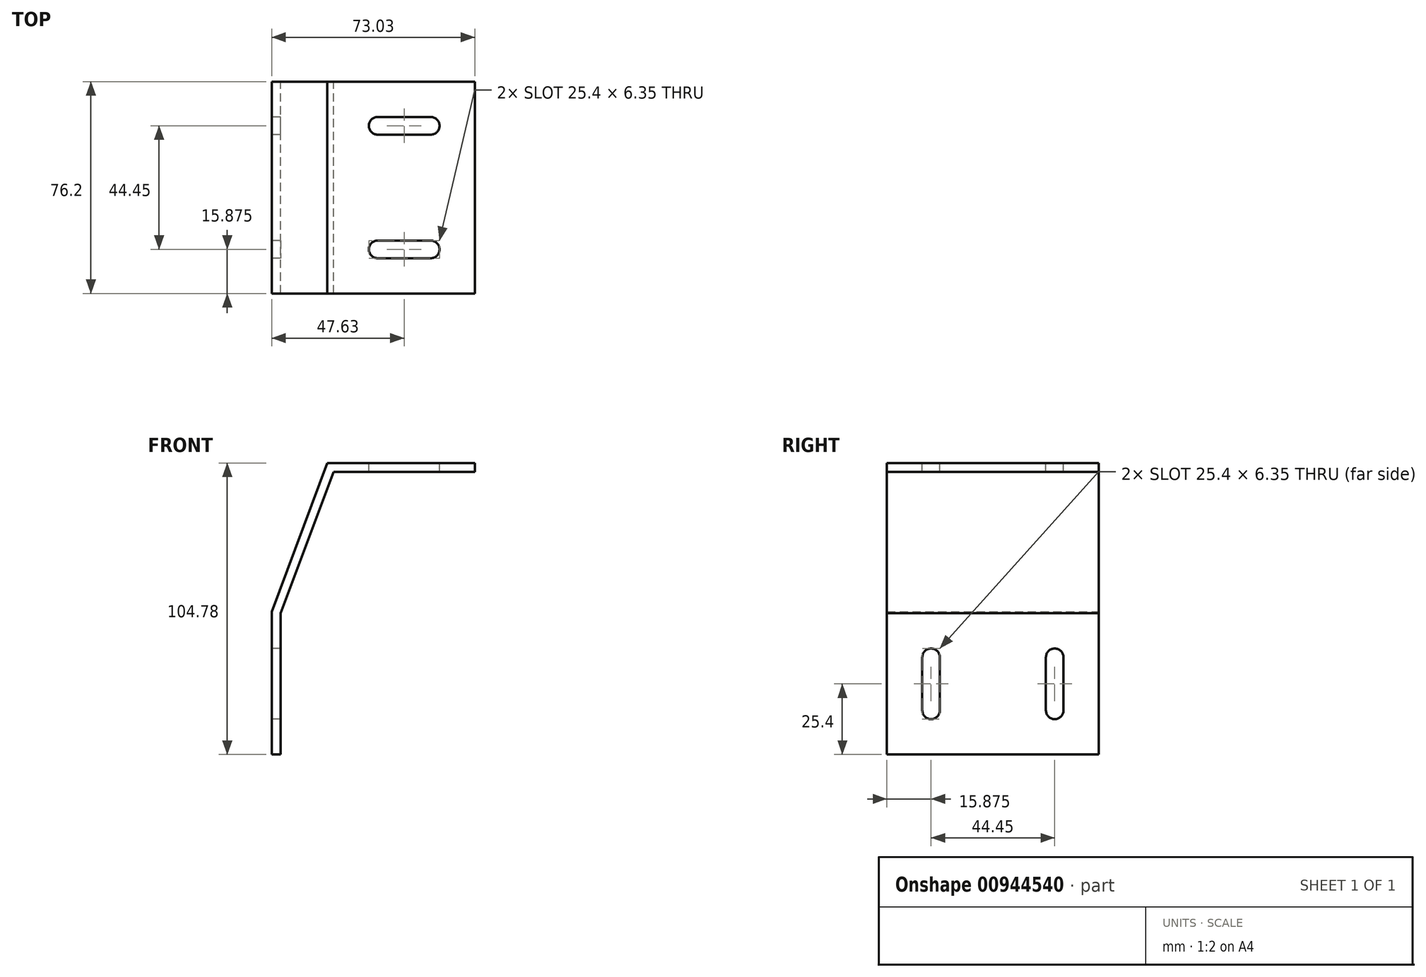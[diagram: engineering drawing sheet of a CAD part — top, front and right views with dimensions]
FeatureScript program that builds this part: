
annotation { "Feature Type Name" : "Feature", "Feature Type Description" : "" }
export const myFeature = defineFeature(function(context is Context, id is Id, definition is map)
    precondition{}
    {
        {
            var Q0;
            Q0=qCreatedBy(makeId("Front.planeOp"),FACE);
            var sketch = newSketch(context, id + "F0", { "sketchPlane" : qUnion([Q0])});
            skLineSegment(sketch, "E0", {"start": v(0, 0) * mm, "end": v(0, -50.8) * mm});
            skLineSegment(sketch, "E1", {"start": v(19.05, 50.8) * mm, "end": v(69.85, 50.8) * mm});
            skLineSegment(sketch, "E2", {"start": v(19.05, 50.8) * mm, "end": v(0, 0) * mm});
            skLineSegment(sketch, "E3", {"start": v(69.85, 50.8) * mm, "end": v(69.85, 53.98) * mm});
            skLineSegment(sketch, "E4", {"start": v(69.85, 53.98) * mm, "end": v(16.85, 53.98) * mm});
            skLineSegment(sketch, "E5", {"start": v(0, -50.8) * mm, "end": v(-3.18, -50.8) * mm});
            skLineSegment(sketch, "E6", {"start": v(-3.18, -50.8) * mm, "end": v(-3.18, 0.58) * mm});
            skLineSegment(sketch, "E7", {"start": v(-3.18, 0.58) * mm, "end": v(16.85, 53.98) * mm});
            skSolve(sketch);
        }
        {
            var Q0;
            Q0=qSketchRegion(id+"F0",true);
            extrude(context, id + "F1", {"entities" : qUnion([Q0]), "depth" : 76.2 * mm, "offsetDistance" : 25.4 * mm});
        }
        {
            var Q0;
            Q0=makeQuery(id+"F1.opExtrude","SWEPT_FACE",FACE,{"disambiguationData":[OSD([sQuery(id+"F0.wireOp",EDGE,"E4")])]});
            var sketch = newSketch(context, id + "F2", { "sketchPlane" : qUnion([Q0])});
            skCircle(sketch, "E8", {"center": v(53.97, -15.87) * mm, "radius": 3.18 * mm});
            skCircle(sketch, "E9", {"center": v(34.92, -15.88) * mm, "radius": 3.18 * mm});
            skLineSegment(sketch, "E10", {"start": v(34.92, -12.7) * mm, "end": v(53.97, -12.7) * mm});
            skLineSegment(sketch, "E11", {"start": v(34.92, -19.05) * mm, "end": v(53.97, -19.05) * mm});
            skCircle(sketch, "E12", {"center": v(53.97, -60.33) * mm, "radius": 3.18 * mm});
            skCircle(sketch, "E13", {"center": v(34.92, -60.33) * mm, "radius": 3.18 * mm});
            skLineSegment(sketch, "E14", {"start": v(34.92, -57.15) * mm, "end": v(53.97, -57.15) * mm});
            skLineSegment(sketch, "E15", {"start": v(34.92, -63.5) * mm, "end": v(53.97, -63.5) * mm});
            skSolve(sketch);
        }
        {
            var Q0;
            {var subQ0=sQuery(id+"F2.wireOp",EDGE,"E8");var subQ1=makeQuery(id+"F2.imprint","INTERSECT",VERTEX,{"derivedFrom":[subQ0,sQuery(id+"F2.wireOp",EDGE,"E10")]});Q0=makeQuery(id+"F2.imprint","IMPRINT",FACE,{"disambiguationData":[TD([[makeQuery(id+"F2.imprint","IMPRINT",EDGE,{"disambiguationData":[TD([[subQ1,-1.0]])],"derivedFrom":subQ0}),1.0]])]});}
            var Q1;
            {var subQ0=sQuery(id+"F2.wireOp",EDGE,"E10");Q1=makeQuery(id+"F2.imprint","IMPRINT",FACE,{"disambiguationData":[TD([[makeQuery(id+"F2.imprint","IMPRINT",EDGE,{"derivedFrom":subQ0}),-1.0]])]});}
            var Q2;
            {var subQ0=sQuery(id+"F2.wireOp",EDGE,"E9");var subQ1=makeQuery(id+"F2.imprint","INTERSECT",VERTEX,{"derivedFrom":[subQ0,sQuery(id+"F2.wireOp",EDGE,"E10")]});Q2=makeQuery(id+"F2.imprint","IMPRINT",FACE,{"disambiguationData":[TD([[makeQuery(id+"F2.imprint","IMPRINT",EDGE,{"disambiguationData":[TD([[subQ1,-1.0]])],"derivedFrom":subQ0}),1.0]])]});}
            extrude(context, id + "F3", {"entities" : qUnion([Q0, Q1, Q2]), "operationType" : NewBodyOperationType.REMOVE, "endBound" : BoundingType.THROUGH_ALL, "oppositeDirection" : true, "depth" : 25.4 * mm, "offsetDistance" : 25.4 * mm});
        }
        {
            var Q0;
            {var subQ0=sQuery(id+"F2.wireOp",EDGE,"E13");var subQ1=makeQuery(id+"F2.imprint","INTERSECT",VERTEX,{"derivedFrom":[subQ0,sQuery(id+"F2.wireOp",EDGE,"E14")]});Q0=makeQuery(id+"F2.imprint","IMPRINT",FACE,{"disambiguationData":[TD([[makeQuery(id+"F2.imprint","IMPRINT",EDGE,{"disambiguationData":[TD([[subQ1,-1.0]])],"derivedFrom":subQ0}),1.0]])]});}
            var Q1;
            {var subQ0=sQuery(id+"F2.wireOp",EDGE,"E12");var subQ1=makeQuery(id+"F2.imprint","INTERSECT",VERTEX,{"derivedFrom":[subQ0,sQuery(id+"F2.wireOp",EDGE,"E14")]});Q1=makeQuery(id+"F2.imprint","IMPRINT",FACE,{"disambiguationData":[TD([[makeQuery(id+"F2.imprint","IMPRINT",EDGE,{"disambiguationData":[TD([[subQ1,-1.0]])],"derivedFrom":subQ0}),1.0]])]});}
            var Q2;
            {var subQ0=sQuery(id+"F2.wireOp",EDGE,"E14");Q2=makeQuery(id+"F2.imprint","IMPRINT",FACE,{"disambiguationData":[TD([[makeQuery(id+"F2.imprint","IMPRINT",EDGE,{"derivedFrom":subQ0}),-1.0]])]});}
            extrude(context, id + "F4", {"entities" : qUnion([Q0, Q1, Q2]), "operationType" : NewBodyOperationType.REMOVE, "endBound" : BoundingType.THROUGH_ALL, "oppositeDirection" : true, "depth" : 25.4 * mm, "offsetDistance" : 25.4 * mm});
        }
        {
            var Q0;
            Q0=makeQuery(id+"F1.opExtrude","SWEPT_FACE",FACE,{"disambiguationData":[OSD([sQuery(id+"F0.wireOp",EDGE,"E6")])]});
            var sketch = newSketch(context, id + "F5", { "sketchPlane" : qUnion([Q0])});
            skLineSegment(sketch, "E16.bottom", {"start": v(12.7, -34.93) * mm, "end": v(19.05, -34.93) * mm});
            skLineSegment(sketch, "E16.top", {"start": v(12.7, -15.88) * mm, "end": v(19.05, -15.88) * mm});
            skLineSegment(sketch, "E16.left", {"start": v(12.7, -34.93) * mm, "end": v(12.7, -15.88) * mm});
            skLineSegment(sketch, "E16.right", {"start": v(19.05, -34.93) * mm, "end": v(19.05, -15.88) * mm});
            skArc(sketch, "E17", {"start": v(19.05, -15.88) * mm, "mid": v(15.88, -12.7) * mm, "end": v(12.7, -15.88) * mm});
            skArc(sketch, "E18", {"start": v(12.7, -34.93) * mm, "mid": v(15.88, -38.1) * mm, "end": v(19.05, -34.93) * mm});
            skSolve(sketch);
        }
        {
            var Q0;
            Q0=makeQuery(id+"F5.imprint","IMPRINT",FACE,{"disambiguationData":[TD([[makeQuery(id+"F5.imprint","IMPRINT",EDGE,{"derivedFrom":sQuery(id+"F5.wireOp",EDGE,"E16.bottom")}),-1.0]])]});
            var Q1;
            Q1=makeQuery(id+"F5.imprint","IMPRINT",FACE,{"disambiguationData":[TD([[makeQuery(id+"F5.imprint","IMPRINT",EDGE,{"derivedFrom":sQuery(id+"F5.wireOp",EDGE,"E16.top")}),1.0]])]});
            var Q2;
            Q2=makeQuery(id+"F5.imprint","IMPRINT",FACE,{"disambiguationData":[TD([[makeQuery(id+"F5.imprint","IMPRINT",EDGE,{"derivedFrom":sQuery(id+"F5.wireOp",EDGE,"E16.bottom")}),1.0]])]});
            extrude(context, id + "F6", {"entities" : qUnion([Q0, Q1, Q2]), "operationType" : NewBodyOperationType.REMOVE, "endBound" : BoundingType.THROUGH_ALL, "oppositeDirection" : true, "depth" : 25.4 * mm, "offsetDistance" : 25.4 * mm});
        }
        {
            var Q0;
            Q0=makeQuery(id+"F1.opExtrude","SWEPT_FACE",FACE,{"disambiguationData":[OSD([sQuery(id+"F0.wireOp",EDGE,"E6")])]});
            var sketch = newSketch(context, id + "F7", { "sketchPlane" : qUnion([Q0])});
            skLineSegment(sketch, "E19.bottom", {"start": v(63.5, -34.93) * mm, "end": v(57.15, -34.93) * mm});
            skLineSegment(sketch, "E19.top", {"start": v(63.5, -15.88) * mm, "end": v(57.15, -15.88) * mm});
            skLineSegment(sketch, "E19.left", {"start": v(63.5, -34.92) * mm, "end": v(63.5, -15.88) * mm});
            skLineSegment(sketch, "E19.right", {"start": v(57.15, -34.92) * mm, "end": v(57.15, -15.88) * mm});
            skArc(sketch, "E20", {"start": v(57.15, -34.92) * mm, "mid": v(60.33, -38.1) * mm, "end": v(63.5, -34.92) * mm});
            skArc(sketch, "E21", {"start": v(63.5, -15.88) * mm, "mid": v(60.33, -12.7) * mm, "end": v(57.15, -15.88) * mm});
            skSolve(sketch);
        }
        {
            var Q0;
            Q0=makeQuery(id+"F7.imprint","IMPRINT",FACE,{"disambiguationData":[TD([[makeQuery(id+"F7.imprint","IMPRINT",EDGE,{"derivedFrom":sQuery(id+"F7.wireOp",EDGE,"E19.top")}),-1.0]])]});
            var Q1;
            Q1=makeQuery(id+"F7.imprint","IMPRINT",FACE,{"disambiguationData":[TD([[makeQuery(id+"F7.imprint","IMPRINT",EDGE,{"derivedFrom":sQuery(id+"F7.wireOp",EDGE,"E19.bottom")}),1.0]])]});
            var Q2;
            Q2=makeQuery(id+"F7.imprint","IMPRINT",FACE,{"disambiguationData":[TD([[makeQuery(id+"F7.imprint","IMPRINT",EDGE,{"derivedFrom":sQuery(id+"F7.wireOp",EDGE,"E19.bottom")}),-1.0]])]});
            extrude(context, id + "F8", {"entities" : qUnion([Q0, Q1, Q2]), "operationType" : NewBodyOperationType.REMOVE, "endBound" : BoundingType.THROUGH_ALL, "oppositeDirection" : true, "depth" : 25.4 * mm, "offsetDistance" : 25.4 * mm});
        }
    });
